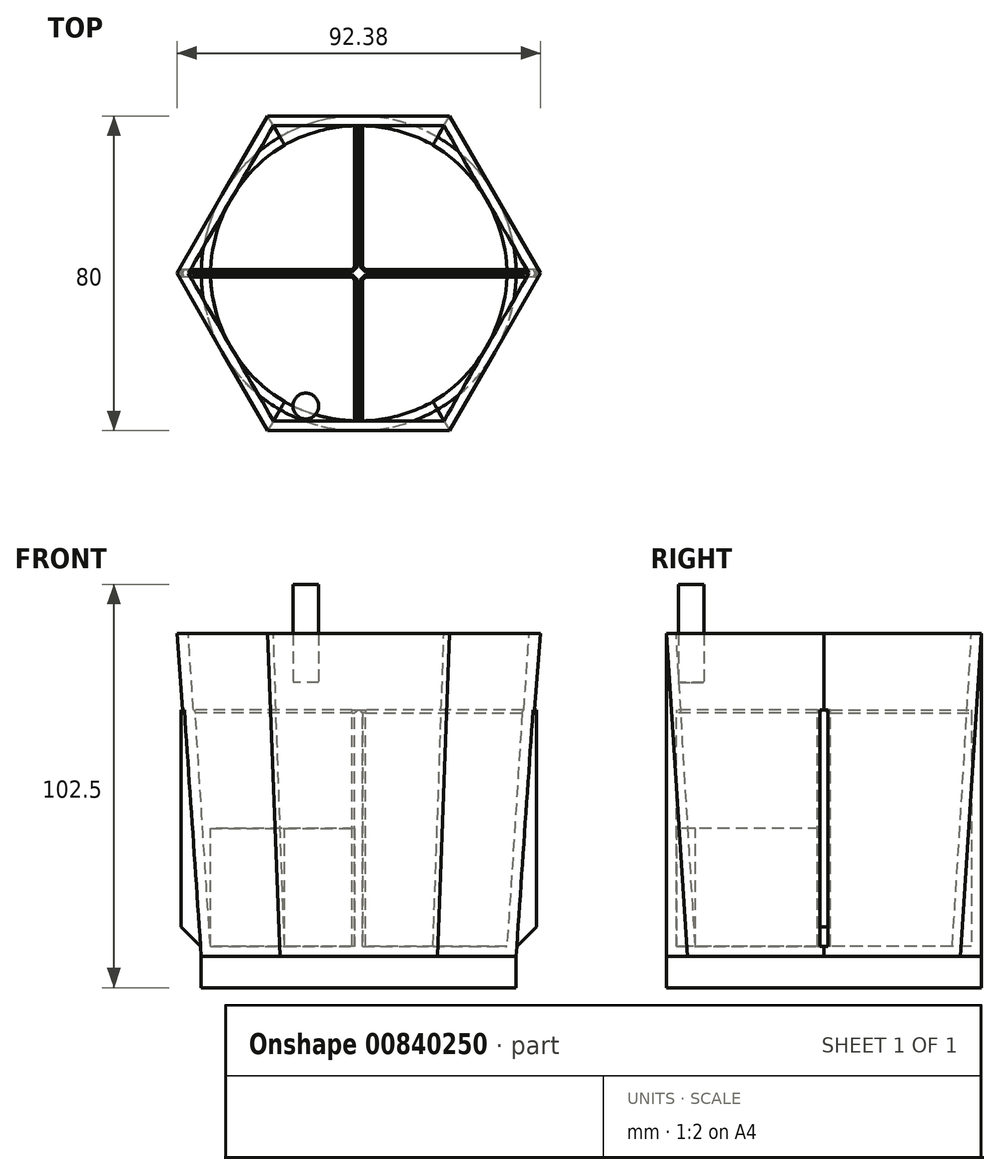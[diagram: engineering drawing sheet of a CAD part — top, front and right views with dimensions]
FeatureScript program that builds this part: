
annotation { "Feature Type Name" : "Feature", "Feature Type Description" : "" }
export const myFeature = defineFeature(function(context is Context, id is Id, definition is map)
    precondition{}
    {
        {
            var Q0;
            Q0=qCreatedBy(makeId("Top.planeOp"),FACE);
            var sketch = newSketch(context, id + "F0", { "sketchPlane" : qUnion([Q0])});
            skCircle(sketch, "E0", {"center": v(0, 0) * mm, "radius": 40 * mm});
            skSolve(sketch);
        }
        {
            var Q0;
            Q0=qCreatedBy(makeId("Top.planeOp"),FACE);
            cPlane(context, id + "F1", {"entities" : qUnion([Q0]), "cplaneType" : CPlaneType.OFFSET, "offset" : 90 * mm, "width" : 150 * mm, "height" : 150 * mm});
        }
        {
            var Q0;
            Q0=qCreatedBy(id+"F1.planeOp",FACE);
            var sketch = newSketch(context, id + "F2", { "sketchPlane" : qUnion([Q0])});
            skCircle(sketch, "E1.cCircle", {"center": v(0, 0) * mm, "radius": 40 * mm, "construction": true});
            skLineSegment(sketch, "E1.0", {"start": v(-23.1, 40) * mm, "end": v(23.1, 40) * mm});
            skLineSegment(sketch, "E1.1", {"start": v(23.1, 40) * mm, "end": v(46.19, 0) * mm});
            skLineSegment(sketch, "E1.2", {"start": v(46.19, 0) * mm, "end": v(23.1, -40) * mm});
            skLineSegment(sketch, "E1.3", {"start": v(23.1, -40) * mm, "end": v(-23.1, -40) * mm});
            skLineSegment(sketch, "E1.4", {"start": v(-23.1, -40) * mm, "end": v(-46.19, 0) * mm});
            skLineSegment(sketch, "E1.5", {"start": v(-46.19, 0) * mm, "end": v(-23.1, 40) * mm});
            skPoint(sketch, "E1.0.midPoint", {"position": v(0, 40) * mm});
            skSolve(sketch);
        }
        {
            var Q0;
            Q0 = qSketchRegion(id + "F0", true);
            extrude(context, id + "F3", {"entities" : qUnion([Q0]), "depth" : 8 * mm, "offsetDistance" : 25 * mm});
        }
        {
            var Q0;
            Q0=makeQuery(id+"F3.opExtrude","CAP_FACE",FACE,{"disambiguationData":[OSD([sQuery(id+"F0.wireOp",EDGE,"E0")])],"isStart":false});
            var sketch = newSketch(context, id + "F4", { "sketchPlane" : qUnion([Q0])});
            skSolve(sketch);
        }
        {
            var Q0;
            Q0=makeQuery(id+"F4.imprint","IMPRINT",FACE,{"disambiguationData":[TD([[makeQuery(id+"F4.imprint","IMPRINT",EDGE,{"derivedFrom":makeQuery(id+"F3.opExtrude","CAP_EDGE",EDGE,{"disambiguationData":[OSD([sQuery(id+"F0.wireOp",EDGE,"E0")])],"isStart":false})}),1.0]])]});
            var Q1;
            Q1=makeQuery(id+"F2.imprint","IMPRINT",FACE,{"disambiguationData":[TD([[makeQuery(id+"F2.imprint","IMPRINT",EDGE,{"derivedFrom":sQuery(id+"F2.wireOp",EDGE,"E1.0")}),-1.0]])]});
            loft(context, id + "F5", {"sheetProfilesArray" : [{ "sheetProfileEntities" : qUnion([Q0]) }, { "sheetProfileEntities" : qUnion([Q1]) }]});
        }
        {
            var Q0;
            Q0=makeQuery(id+"F5.opLoft","CAP_FACE",FACE,{"disambiguationData":[OSD([makeQuery(id+"F2.imprint","IMPRINT",FACE,{"disambiguationData":[TD([[makeQuery(id+"F2.imprint","IMPRINT",EDGE,{"derivedFrom":sQuery(id+"F2.wireOp",EDGE,"E1.0")}),-1.0]])]})])],"isStart":true});
            shell(context, id + "F6", {"entities" : qUnion([Q0]), "thickness" : 2.5 * mm});
        }
        {
            var Q0;
            Q0=makeQuery(id+"F6.opShell","OFFSET_FACE",FACE,{"disambiguationData":[OSD([makeQuery(id+"F4.imprint","IMPRINT",FACE,{"disambiguationData":[TD([[makeQuery(id+"F4.imprint","IMPRINT",EDGE,{"derivedFrom":makeQuery(id+"F3.opExtrude","CAP_EDGE",EDGE,{"disambiguationData":[OSD([sQuery(id+"F0.wireOp",EDGE,"E0")])],"isStart":false})}),1.0]])]})])]});
            var sketch = newSketch(context, id + "F7", { "sketchPlane" : qUnion([Q0])});
            skLineSegment(sketch, "E2.bottom", {"start": v(-1, 39.83) * mm, "end": v(1, 39.83) * mm});
            skLineSegment(sketch, "E2.top", {"start": v(-1, -39.83) * mm, "end": v(1, -39.83) * mm});
            skLineSegment(sketch, "E2.left", {"start": v(-1, 39.83) * mm, "end": v(-1, -39.83) * mm});
            skLineSegment(sketch, "E2.right", {"start": v(1, 39.83) * mm, "end": v(1, -39.83) * mm});
            skPoint(sketch, "E2.middle", {"position": v(0, 0) * mm});
            skLineSegment(sketch, "E3.bottom", {"start": v(45.15, 1) * mm, "end": v(-45.15, 1) * mm});
            skLineSegment(sketch, "E3.top", {"start": v(45.15, -1) * mm, "end": v(-45.15, -1) * mm});
            skLineSegment(sketch, "E3.left", {"start": v(45.15, 1) * mm, "end": v(45.15, -1) * mm});
            skLineSegment(sketch, "E3.right", {"start": v(-45.15, 1) * mm, "end": v(-45.15, -1) * mm});
            skSolve(sketch);
        }
        {
            var Q0;
            Q0 = qSketchRegion(id + "F7", true);
            extrude(context, id + "F8", {"entities" : qUnion([Q0]), "operationType" : NewBodyOperationType.ADD, "depth" : 60 * mm, "offsetDistance" : 25 * mm});
        }
        {
            var Q0;
            {var subQ0=sQuery(id+"F2.wireOp",EDGE,"E1.5");var subQ1=sQuery(id+"F2.wireOp",EDGE,"E1.0");var subQ2=sQuery(id+"F0.wireOp",EDGE,"E0");var subQ3=sQuery(id+"F7.wireOp",EDGE,"E3.bottom");var subQ4=sQuery(id+"F7.wireOp",EDGE,"E2.left");var subQ5=makeQuery(id+"F7.imprint","INTERSECT",VERTEX,{"derivedFrom":[subQ4,subQ3]});var subQ8=sQuery(id+"F7.wireOp",EDGE,"E3.right");var subQ10=makeQuery(id+"F7.imprint","IMPRINT",EDGE,{"disambiguationData":[TD([[makeQuery(id+"F7.imprint","INTERSECT",VERTEX,{"derivedFrom":[subQ3,subQ8]}),1.0]])],"derivedFrom":subQ3});var subQ11=makeQuery(id+"F7.imprint","IMPRINT",EDGE,{"disambiguationData":[TD([[subQ5,-1.0]])],"derivedFrom":subQ3});Q0=makeQuery(id+"F8.boolean.opBoolean","SPLIT",EDGE,{"disambiguationData":[TD([makeQuery(id+"F6.opShell","OFFSET_FACE",FACE,{"disambiguationData":[OSD([subQ2,subQ1,sQuery(id+"F2.wireOp",EDGE,"E1.4"),subQ0])]})])],"derivedFrom":makeQuery(id+"F8.opExtrude","CAP_EDGE",EDGE,{"disambiguationData":[OSD([subQ3]),TDD([subQ11,subQ10])],"isStart":false})});}
            var Q1;
            {var subQ0=sQuery(id+"F2.wireOp",EDGE,"E1.5");var subQ1=sQuery(id+"F2.wireOp",EDGE,"E1.4");var subQ2=sQuery(id+"F2.wireOp",EDGE,"E1.3");var subQ3=sQuery(id+"F2.wireOp",EDGE,"E1.0");var subQ4=sQuery(id+"F0.wireOp",EDGE,"E0");var subQ5=sQuery(id+"F7.wireOp",EDGE,"E3.right");var subQ6=sQuery(id+"F7.wireOp",EDGE,"E3.top");var subQ7=sQuery(id+"F7.wireOp",EDGE,"E2.left");var subQ10=makeQuery(id+"F7.imprint","INTERSECT",VERTEX,{"derivedFrom":[subQ7,subQ6]});var subQ12=makeQuery(id+"F7.imprint","IMPRINT",EDGE,{"disambiguationData":[TD([[makeQuery(id+"F7.imprint","INTERSECT",VERTEX,{"derivedFrom":[subQ6,subQ5]}),1.0]])],"derivedFrom":subQ6});var subQ13=makeQuery(id+"F7.imprint","IMPRINT",EDGE,{"disambiguationData":[TD([[subQ10,-1.0]])],"derivedFrom":subQ6});Q1=makeQuery(id+"F8.boolean.opBoolean","SPLIT",EDGE,{"disambiguationData":[TD([makeQuery(id+"F6.opShell","OFFSET_FACE",FACE,{"disambiguationData":[OSD([subQ4,subQ3,subQ2,subQ1,subQ0])]})])],"derivedFrom":makeQuery(id+"F8.opExtrude","CAP_EDGE",EDGE,{"disambiguationData":[OSD([subQ6]),TDD([subQ13,subQ12])],"isStart":false})});}
            var Q2;
            {var subQ5=sQuery(id+"F7.wireOp",EDGE,"E3.right");var subQ6=sQuery(id+"F7.wireOp",EDGE,"E3.bottom");var subQ7=sQuery(id+"F7.wireOp",EDGE,"E2.left");var subQ8=sQuery(id+"F7.wireOp",EDGE,"E2.bottom");var subQ9=makeQuery(id+"F7.imprint","INTERSECT",VERTEX,{"derivedFrom":[subQ7,subQ6]});var subQ11=makeQuery(id+"F7.imprint","IMPRINT",EDGE,{"disambiguationData":[TD([[subQ9,1.0]])],"derivedFrom":subQ7});var subQ12=makeQuery(id+"F7.imprint","IMPRINT",EDGE,{"disambiguationData":[TD([[makeQuery(id+"F7.imprint","INTERSECT",VERTEX,{"derivedFrom":[subQ8,subQ7]}),-1.0]])],"derivedFrom":subQ7});Q2=makeQuery(id+"F8.boolean.opBoolean","SPLIT",EDGE,{"disambiguationData":[TD([makeQuery(id+"F8.opExtrude","SWEPT_FACE",FACE,{"disambiguationData":[OSD([subQ6]),TDD([makeQuery(id+"F7.imprint","IMPRINT",EDGE,{"disambiguationData":[TD([[subQ9,-1.0]])],"derivedFrom":subQ6}),makeQuery(id+"F7.imprint","IMPRINT",EDGE,{"disambiguationData":[TD([[makeQuery(id+"F7.imprint","INTERSECT",VERTEX,{"derivedFrom":[subQ6,subQ5]}),1.0]])],"derivedFrom":subQ6})])]})])],"derivedFrom":makeQuery(id+"F8.opExtrude","CAP_EDGE",EDGE,{"disambiguationData":[OSD([subQ7]),TDD([subQ12,subQ11])],"isStart":false})});}
            var Q3;
            {var subQ0=sQuery(id+"F2.wireOp",EDGE,"E1.5");var subQ1=sQuery(id+"F2.wireOp",EDGE,"E1.2");var subQ2=sQuery(id+"F2.wireOp",EDGE,"E1.1");var subQ3=sQuery(id+"F2.wireOp",EDGE,"E1.0");var subQ4=sQuery(id+"F0.wireOp",EDGE,"E0");var subQ6=sQuery(id+"F7.wireOp",EDGE,"E3.bottom");var subQ7=sQuery(id+"F7.wireOp",EDGE,"E2.right");var subQ8=sQuery(id+"F7.wireOp",EDGE,"E2.bottom");var subQ9=makeQuery(id+"F7.imprint","INTERSECT",VERTEX,{"derivedFrom":[subQ7,subQ6]});var subQ11=makeQuery(id+"F7.imprint","IMPRINT",EDGE,{"disambiguationData":[TD([[subQ9,1.0]])],"derivedFrom":subQ7});var subQ12=makeQuery(id+"F7.imprint","IMPRINT",EDGE,{"disambiguationData":[TD([[makeQuery(id+"F7.imprint","INTERSECT",VERTEX,{"derivedFrom":[subQ8,subQ7]}),-1.0]])],"derivedFrom":subQ7});Q3=makeQuery(id+"F8.boolean.opBoolean","SPLIT",EDGE,{"disambiguationData":[TD([makeQuery(id+"F6.opShell","OFFSET_FACE",FACE,{"disambiguationData":[OSD([subQ4,subQ3,subQ2,subQ1,subQ0])]})])],"derivedFrom":makeQuery(id+"F8.opExtrude","CAP_EDGE",EDGE,{"disambiguationData":[OSD([subQ7]),TDD([subQ12,subQ11])],"isStart":false})});}
            var Q4;
            {var subQ0=sQuery(id+"F2.wireOp",EDGE,"E1.4");var subQ1=sQuery(id+"F2.wireOp",EDGE,"E1.3");var subQ2=sQuery(id+"F2.wireOp",EDGE,"E1.2");var subQ3=sQuery(id+"F0.wireOp",EDGE,"E0");var subQ4=sQuery(id+"F7.wireOp",EDGE,"E3.left");var subQ5=sQuery(id+"F7.wireOp",EDGE,"E3.top");var subQ6=sQuery(id+"F7.wireOp",EDGE,"E2.right");var subQ10=makeQuery(id+"F7.imprint","INTERSECT",VERTEX,{"derivedFrom":[subQ6,subQ5]});var subQ12=makeQuery(id+"F7.imprint","IMPRINT",EDGE,{"disambiguationData":[TD([[subQ10,1.0]])],"derivedFrom":subQ5});var subQ13=makeQuery(id+"F7.imprint","IMPRINT",EDGE,{"disambiguationData":[TD([[makeQuery(id+"F7.imprint","INTERSECT",VERTEX,{"derivedFrom":[subQ5,subQ4]}),-1.0]])],"derivedFrom":subQ5});Q4=makeQuery(id+"F8.boolean.opBoolean","SPLIT",EDGE,{"disambiguationData":[TD([makeQuery(id+"F6.opShell","OFFSET_FACE",FACE,{"disambiguationData":[OSD([subQ3,sQuery(id+"F2.wireOp",EDGE,"E1.1"),subQ2,subQ1,subQ0])]})])],"derivedFrom":makeQuery(id+"F8.opExtrude","CAP_EDGE",EDGE,{"disambiguationData":[OSD([subQ5]),TDD([subQ13,subQ12])],"isStart":false})});}
            var Q5;
            {var subQ0=sQuery(id+"F2.wireOp",EDGE,"E1.5");var subQ1=sQuery(id+"F2.wireOp",EDGE,"E1.4");var subQ2=sQuery(id+"F2.wireOp",EDGE,"E1.3");var subQ3=sQuery(id+"F2.wireOp",EDGE,"E1.2");var subQ4=sQuery(id+"F0.wireOp",EDGE,"E0");var subQ6=sQuery(id+"F7.wireOp",EDGE,"E3.top");var subQ7=sQuery(id+"F7.wireOp",EDGE,"E2.right");var subQ8=sQuery(id+"F7.wireOp",EDGE,"E2.top");var subQ10=makeQuery(id+"F7.imprint","IMPRINT",EDGE,{"disambiguationData":[TD([[makeQuery(id+"F7.imprint","INTERSECT",VERTEX,{"derivedFrom":[subQ8,subQ7]}),1.0]])],"derivedFrom":subQ7});var subQ11=makeQuery(id+"F7.imprint","INTERSECT",VERTEX,{"derivedFrom":[subQ7,subQ6]});var subQ12=makeQuery(id+"F7.imprint","IMPRINT",EDGE,{"disambiguationData":[TD([[subQ11,-1.0]])],"derivedFrom":subQ7});Q5=makeQuery(id+"F8.boolean.opBoolean","SPLIT",EDGE,{"disambiguationData":[TD([makeQuery(id+"F6.opShell","OFFSET_FACE",FACE,{"disambiguationData":[OSD([subQ4,subQ3,subQ2,subQ1,subQ0])]})])],"derivedFrom":makeQuery(id+"F8.opExtrude","CAP_EDGE",EDGE,{"disambiguationData":[OSD([subQ7]),TDD([subQ12,subQ10])],"isStart":false})});}
            var Q6;
            {var subQ0=sQuery(id+"F2.wireOp",EDGE,"E1.5");var subQ1=sQuery(id+"F2.wireOp",EDGE,"E1.4");var subQ2=sQuery(id+"F2.wireOp",EDGE,"E1.3");var subQ3=sQuery(id+"F0.wireOp",EDGE,"E0");var subQ5=sQuery(id+"F7.wireOp",EDGE,"E3.top");var subQ6=sQuery(id+"F7.wireOp",EDGE,"E2.left");var subQ7=sQuery(id+"F7.wireOp",EDGE,"E2.top");var subQ9=makeQuery(id+"F7.imprint","IMPRINT",EDGE,{"disambiguationData":[TD([[makeQuery(id+"F7.imprint","INTERSECT",VERTEX,{"derivedFrom":[subQ7,subQ6]}),1.0]])],"derivedFrom":subQ6});var subQ10=makeQuery(id+"F7.imprint","INTERSECT",VERTEX,{"derivedFrom":[subQ6,subQ5]});var subQ11=makeQuery(id+"F7.imprint","IMPRINT",EDGE,{"disambiguationData":[TD([[subQ10,-1.0]])],"derivedFrom":subQ6});Q6=makeQuery(id+"F8.boolean.opBoolean","SPLIT",EDGE,{"disambiguationData":[TD([makeQuery(id+"F6.opShell","OFFSET_FACE",FACE,{"disambiguationData":[OSD([subQ3,sQuery(id+"F2.wireOp",EDGE,"E1.2"),subQ2,subQ1,subQ0])]})])],"derivedFrom":makeQuery(id+"F8.opExtrude","CAP_EDGE",EDGE,{"disambiguationData":[OSD([subQ6]),TDD([subQ11,subQ9])],"isStart":false})});}
            var Q7;
            Q7=makeQuery(id+"F8.opExtrude","SWEPT_EDGE",EDGE,{"disambiguationData":[OSD([sQuery(id+"F7.wireOp",EDGE,"E2.right"),sQuery(id+"F7.wireOp",EDGE,"E3.top")])]});
            var Q8;
            Q8=makeQuery(id+"F8.opExtrude","SWEPT_EDGE",EDGE,{"disambiguationData":[OSD([sQuery(id+"F7.wireOp",EDGE,"E2.right"),sQuery(id+"F7.wireOp",EDGE,"E3.bottom")])]});
            var Q9;
            Q9=makeQuery(id+"F8.opExtrude","SWEPT_EDGE",EDGE,{"disambiguationData":[OSD([sQuery(id+"F7.wireOp",EDGE,"E2.left"),sQuery(id+"F7.wireOp",EDGE,"E3.bottom")])]});
            var Q10;
            Q10=makeQuery(id+"F8.opExtrude","SWEPT_EDGE",EDGE,{"disambiguationData":[OSD([sQuery(id+"F7.wireOp",EDGE,"E2.left"),sQuery(id+"F7.wireOp",EDGE,"E3.top")])]});
            chamfer(context, id + "F9", {"entities" : qUnion([Q0, Q1, Q2, Q3, Q4, Q5, Q6, Q7, Q8, Q9, Q10]), "width" : 0.7 * mm, "tangentPropagation" : true});
        }
        {
            var Q0;
            Q0=makeQuery(id+"F8.opExtrude","CAP_EDGE",EDGE,{"disambiguationData":[OSD([sQuery(id+"F7.wireOp",EDGE,"E3.right")])],"isStart":true});
            var Q1;
            Q1=makeQuery(id+"F8.opExtrude","CAP_EDGE",EDGE,{"disambiguationData":[OSD([sQuery(id+"F7.wireOp",EDGE,"E3.left")])],"isStart":true});
            chamfer(context, id + "F10", {"entities" : qUnion([Q0, Q1]), "width" : 5 * mm, "tangentPropagation" : true});
        }
        {
            var Q0;
            {var subQ0=sQuery(id+"F7.wireOp",EDGE,"E3.top");var subQ1=sQuery(id+"F7.wireOp",EDGE,"E2.left");var subQ2=makeQuery(id+"F7.imprint","INTERSECT",VERTEX,{"derivedFrom":[subQ1,subQ0]});Q0=makeQuery(id+"F7.imprint","IMPRINT",FACE,{"disambiguationData":[TD([[makeQuery(id+"F7.imprint","IMPRINT",EDGE,{"disambiguationData":[TD([[subQ2,-1.0]])],"derivedFrom":subQ1}),-1.0]])]});}
            var sketch = newSketch(context, id + "F11", { "sketchPlane" : qUnion([Q0])});
            skCircle(sketch, "E4", {"center": v(-15.8, -15.42) * mm, "radius": 12.89 * mm});
            skSolve(sketch);
        }
        {
            var Q0;
            {var subQ0=sQuery(id+"F7.wireOp",EDGE,"E3.top");var subQ1=sQuery(id+"F7.wireOp",EDGE,"E2.left");var subQ2=makeQuery(id+"F7.imprint","INTERSECT",VERTEX,{"derivedFrom":[subQ1,subQ0]});Q0=makeQuery(id+"F7.imprint","IMPRINT",FACE,{"disambiguationData":[TD([[makeQuery(id+"F7.imprint","IMPRINT",EDGE,{"disambiguationData":[TD([[subQ2,-1.0]])],"derivedFrom":subQ1}),-1.0]])]});}
            var Q1;
            Q1=sQuery(id+"F11.wireOp",EDGE,"E4");
            extrude(context, id + "F12", {"entities" : qUnion([Q0]), "surfaceEntities" : qUnion([Q1]), "depth" : 30 * mm, "offsetDistance" : 25 * mm});
        }
        {
            var Q0;
            Q0=qCreatedBy(id+"F1.planeOp",FACE);
            var sketch = newSketch(context, id + "F13", { "sketchPlane" : qUnion([Q0])});
            skCircle(sketch, "E5", {"center": v(-13.45, -33.72) * mm, "radius": 3.27 * mm});
            skSolve(sketch);
        }
        {
            var Q0;
            Q0 = qSketchRegion(id + "F13", true);
            extrude(context, id + "F14", {"entities" : qUnion([Q0]), "endBound" : BoundingType.SYMMETRIC, "depth" : 25 * mm, "offsetDistance" : 25 * mm});
        }
    });
